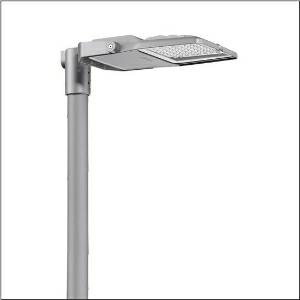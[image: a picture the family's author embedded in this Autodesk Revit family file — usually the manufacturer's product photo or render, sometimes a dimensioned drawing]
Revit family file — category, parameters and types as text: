
# Revit family: floodlight_fl_21_iq_mini___pl33t_5xa7771b2f3a_2789
name_source: partatom
category: Lighting Fixtures
units: mm (PartAtom-declared; Revit-internal decimal feet)

## family parameters
Cut with Voids When Loaded = No
Host = Face
Light Source = No
Part Type = Normal
Room Calculation Point = No
Round Connector Dimension = Use Diameter
Shared = No

## types (1)
- --- (1 x LED, 6170 lm, 45.5 W, 3000K)
    Apparent Load = 46 VA
    CIE Flux Codes = 26 75 99 100 100
    Color Rendering = 70
    Color Temperature = 3000K
    Default Elevation = 1800 mm
    Description = Floodlight FL 21 iQ mini, floodlight, primary light control with lens, of PMMA, primary optical cover: protective disc, of toughened safety glass, transparent, light distribution: PL33T, light emission: direct distribution, installation type: surface-mounted, LED, High Power LED, rated luminous flux: 6.170lm, luminous efficacy: 136lm/W, light colour: 730, colour temperature: 3000K, control gear: iQ Comfort/DALI, control: Auto-Match, Temp-Guard, Lumen-Switch, Night-Set, Smart-Wire, Light-Fading, Desk-Remote (wireless, voltage-free reading and setting of iQ features in the workshop via application-optimized NFC function/RFID function), optimised constant luminous flux control (CLO 2.0), with terminal, 6-pole, mains connection: 220..240V, AC, 50/60Hz, start of lifetime: 46W, end of service life: 48W, reduction: 22W, luminaire housing, of diecast aluminium, powder-coated, Siteco® metallic grey (DB 702S), corrosivity category C5 mid according to DIN EN ISO 12944, suitable for swimming pools, chlorine-resistant, sealing non-destructively replaceable, please order mast flange separately, mast bracket, of steel, galvanised, powder-coated, Siteco® metallic grey (DB 702S), protection rating (complete): IP66, insulation class (complete): insulation class II (safety insulation), certification: CE, ENEC, VDE, protection symbol: D, impact resistance: IK08, permissible operating ambient temperature: -40..+40°C, permissible operating ambient temperature for outdoor applications: -40..+50°C, standard: DIN EN 12944, LABS conformity tested according to VDMA 24364:2018-05, packaging unit: 1 piece

Light Distribution: PL33T
    Height = 70 mm
    Lamp = 1 x LED
    Lamp Light Flux = 6170 lm
    Lamp Power = 45.5 W
    Lamp count = 1
    Length = 485 mm
    Luminous efficacy = 136 lm/W
    Manufacturer = Siteco
    ModVariant = No
    Model = 5XA7771B2F3A
    Number of Poles = 1
    OnlyDefault = Yes
    Power Factor = 1
    Product Name = Floodlight FL 21 iQ mini | PL33T
    Product group = floodlight | pylon annexe
    ProductGroupID = 6200
    Protection Class = Protection class II
    Protection Degree = IP 66
    RLX_Detail_Level = 1
    RLX_Emergency_Light_Flux = 0 lm
    RLX_Emergency_Type = 0
    RLX_Emergency_Type_DB = No
    RlxData = <blob elided: 101245 chars, md5=1181bb1e>
    Socket = socket
    Standby Power = 0 W
    System Light Flux = 6170 lm
    System Power = 46 W
    Type Comments = factory setting: luminous flux: 100 % | dim-lin: 254 | 463 mA
    Type Image = l_1007125.jpg
    URL = http://relux.com
    VarID = @adj_150284
    Voltage = 0 V
    Weight = 0.00 kg
    Width = 337 mm

## geometry (parser evidence)
native form markers: Blend x4, Sweep x11
no freeform markers — native parametric forms only
